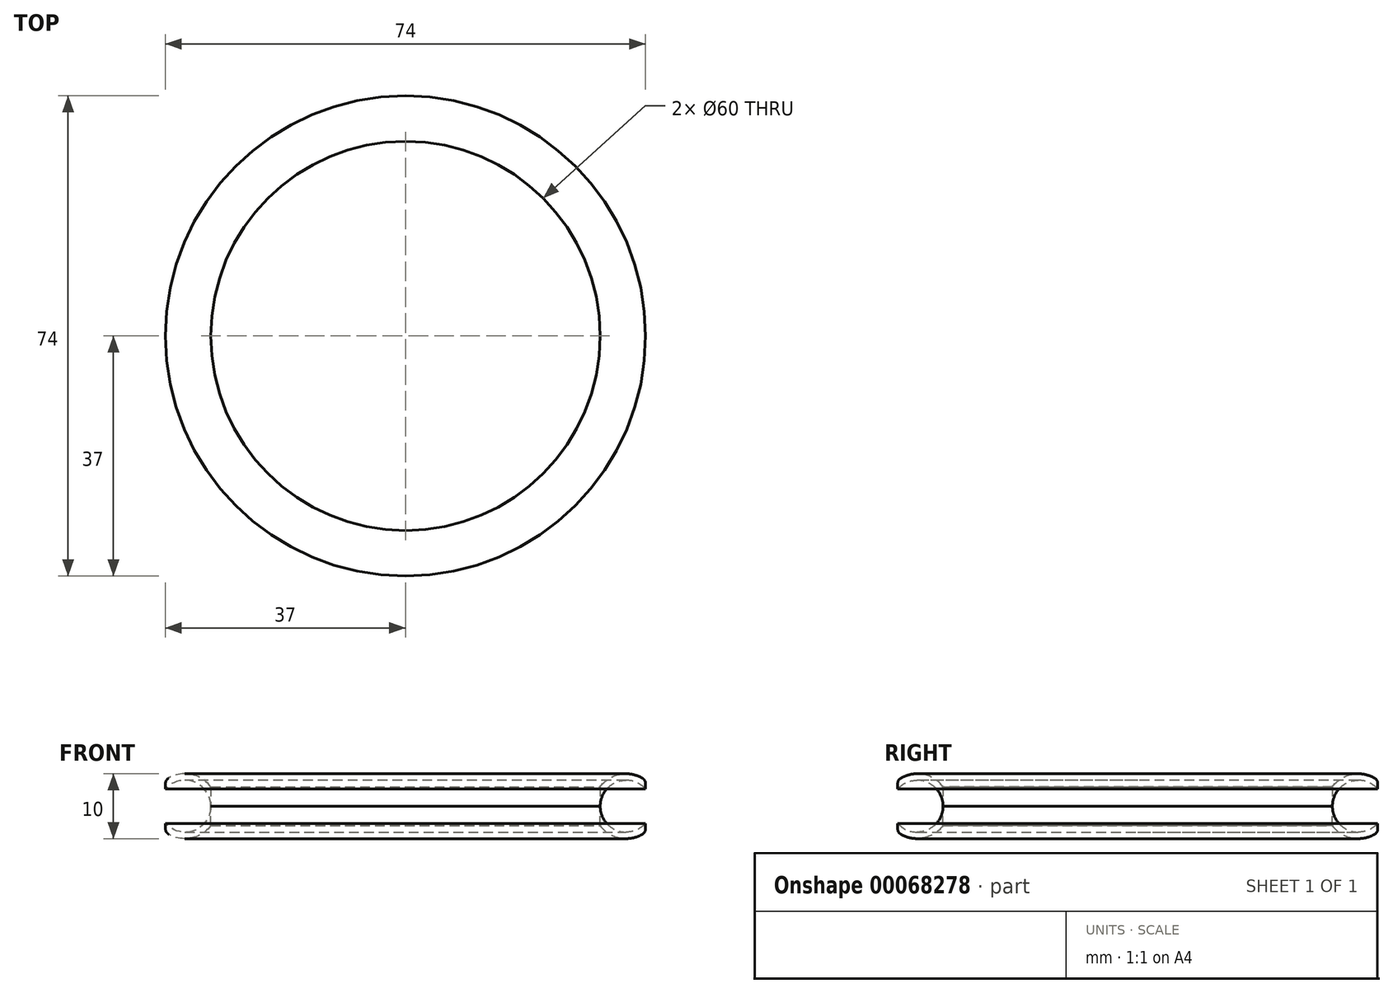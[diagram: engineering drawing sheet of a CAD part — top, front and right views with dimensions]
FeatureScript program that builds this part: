
annotation { "Feature Type Name" : "Feature", "Feature Type Description" : "" }
export const myFeature = defineFeature(function(context is Context, id is Id, definition is map)
    precondition{}
    {
        {
            var Q0;
            Q0=qCreatedBy(makeId("Front.planeOp"),FACE);
            var sketch = newSketch(context, id + "F0", { "sketchPlane" : qUnion([Q0])});
            skLineSegment(sketch, "E0", {"start": v(0, 0) * mm, "end": v(30, 0) * mm, "construction": true});
            skLineSegment(sketch, "E1", {"start": v(30, 0) * mm, "end": v(34, 0) * mm, "construction": true});
            skLineSegment(sketch, "E2", {"start": v(34, 0) * mm, "end": v(37, 0) * mm, "construction": true});
            skLineSegment(sketch, "E3", {"start": v(30, 0) * mm, "end": v(30, 3) * mm});
            skLineSegment(sketch, "E4", {"start": v(30, 0) * mm, "end": v(30, -3) * mm});
            skLineSegment(sketch, "E5", {"start": v(37, 0) * mm, "end": v(37, 4) * mm});
            skLineSegment(sketch, "E6", {"start": v(37, 0) * mm, "end": v(37, 0) * mm});
            skLineSegment(sketch, "E7", {"start": v(30, 3) * mm, "end": v(30, 26.31) * mm});
            skLineSegment(sketch, "E8", {"start": v(30, -3) * mm, "end": v(30, -3) * mm});
            skLineSegment(sketch, "E9", {"start": v(30, -3) * mm, "end": v(30, -28.6) * mm});
            skArc(sketch, "E10", {"start": v(37, -4) * mm, "mid": v(39, 0) * mm, "end": v(37, 4) * mm, "construction": true});
            skLineSegment(sketch, "E11", {"start": v(30, 3) * mm, "end": v(30, 3) * mm});
            skLineSegment(sketch, "E12", {"start": v(37, 4) * mm, "end": v(37, 4) * mm});
            skArc(sketch, "E13", {"start": v(30, 3) * mm, "mid": v(29, 0) * mm, "end": v(30, -3) * mm, "construction": true});
            skArc(sketch, "E14", {"start": v(37, 4) * mm, "mid": v(33.3, 4.95) * mm, "end": v(30, 3) * mm});
            skArc(sketch, "E15", {"start": v(30, -3) * mm, "mid": v(33.3, -4.95) * mm, "end": v(37, -4) * mm});
            skLineSegment(sketch, "E16", {"start": v(37, -4) * mm, "end": v(37, -28.6) * mm});
            skLineSegment(sketch, "E17", {"start": v(37, 0) * mm, "end": v(37, -4) * mm});
            skLineSegment(sketch, "E18", {"start": v(37, 4) * mm, "end": v(37, 28.86) * mm});
            skLineSegment(sketch, "E19", {"start": v(0, 0) * mm, "end": v(0, 13.8) * mm, "construction": true});
            skCircle(sketch, "E20", {"center": v(34, 0) * mm, "radius": 4 * mm});
            skSolve(sketch);
        }
        {
            var Q0;
            Q0=makeQuery(id+"F0.imprint","IMPRINT",FACE,{"disambiguationData":[TD([[makeQuery(id+"F0.imprint","IMPRINT",EDGE,{"derivedFrom":sQuery(id+"F0.wireOp",EDGE,"E3")}),-1.0]])]});
            var Q1;
            Q1=sQuery(id+"F0.wireOp",EDGE,"E19");
            revolve(context, id + "F1", {"entities" : qUnion([Q0]), "axis" : qUnion([Q1]), "revolveType" : RevolveType.FULL});
        }
        {
            var Q0;
            Q0=makeQuery(id+"F1.opRevolve","SWEPT_BODY",BODY,{"disambiguationData":[OSD([sQuery(id+"F0.wireOp",EDGE,"E3"),sQuery(id+"F0.wireOp",EDGE,"E5"),sQuery(id+"F0.wireOp",EDGE,"E14"),sQuery(id+"F0.wireOp",EDGE,"E20")])]});
            var Q1;
            Q1=qCreatedBy(makeId("Top.planeOp"),FACE);
            mirror(context, id + "F2", {"entities" : qUnion([Q0]), "mirrorPlane" : qUnion([Q1])});
        }
        {
            var Q0;
            Q0=makeQuery(id+"F1.opRevolve","SWEPT_EDGE",EDGE,{"disambiguationData":[OSD([sQuery(id+"F0.wireOp",EDGE,"E5"),sQuery(id+"F0.wireOp",EDGE,"E14")])]});
            var Q1;
            Q1=makeQuery(id+"F2.opPattern","COPY",EDGE,{"derivedFrom":makeQuery(id+"F1.opRevolve","SWEPT_EDGE",EDGE,{"disambiguationData":[OSD([sQuery(id+"F0.wireOp",EDGE,"E5"),sQuery(id+"F0.wireOp",EDGE,"E14")])]}),"instanceName":"1"});
            fillet(context, id + "F3", {"entities" : qUnion([Q0, Q1]), "radius" : 1 * mm, "tangentPropagation" : true, "allowEdgeOverflow" : false});
        }
    });
